# Revit family: NLRS_57_AIR_UN_exhaust-deflektor-hood vdk_LT_velu
name_source: partatom
category: Air Terminals
units: mm (PartAtom-declared; Revit-internal decimal feet)

## family parameters
Always vertical = No
Cut with Voids When Loaded = No
Part Type = Normal
Room Calculation Point = No
Round Connector Dimension = Use Diameter
Shared = No
Work Plane-Based = No

## types (1)
- Deflectorkap
    Assembly Code = 57.00
    Description = Velu uitblaas deflectorkap, type VDK
    FireRating = 00
    IfcDescription = Velu uitblaas deflectorkap, type VDK
    IfcExportAs = IfcAirterminal
    IfcExportType = Diffuser
    IsExternal = Yes
    LT = VDK_Data
    LoadBearing = No
    Manufacturer = Velu Ventilatietechniek BV
    Model = VDK
    NLRS_C_content_datum_uitgifte = 25-05-2022
    NLRS_C_content_provider = Velu Ventliatietechniek BV
    NLRS_C_content_versie = 3.19.00
    NLRS_C_description = Velu uitblaas deflectorkap, type VDK
    NLRS_C_niveau ontwikkeling = LOD400
    SACS_Angle1 = 26.57°
    URL = https://velu.nl

## geometry (parser evidence)
native form markers: Sweep x8
no freeform markers — native parametric forms only
